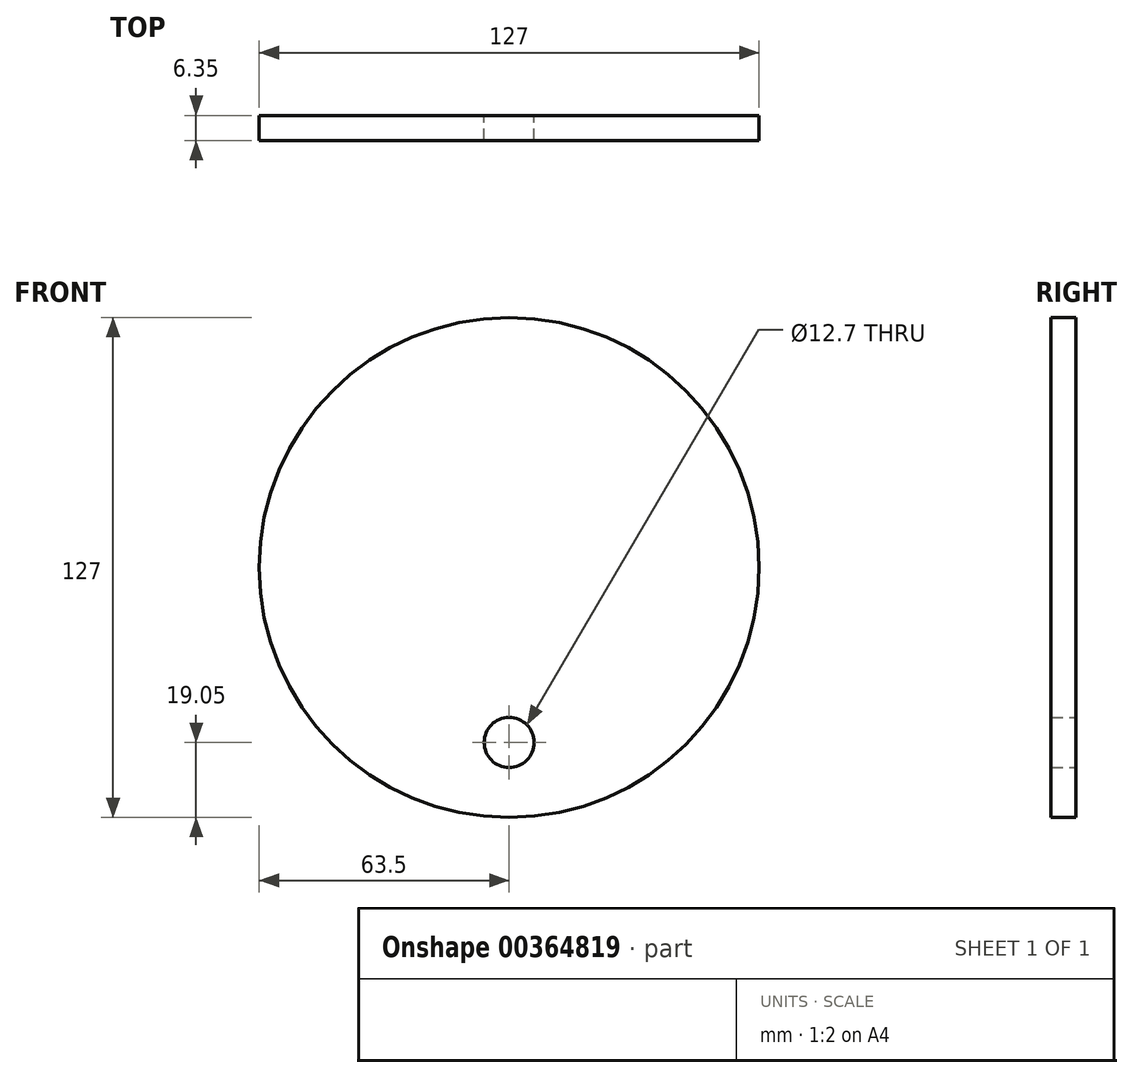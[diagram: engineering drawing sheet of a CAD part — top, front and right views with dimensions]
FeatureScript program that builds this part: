
annotation { "Feature Type Name" : "Feature", "Feature Type Description" : "" }
export const myFeature = defineFeature(function(context is Context, id is Id, definition is map)
    precondition{}
    {
        {
            var Q0;
            Q0=qCreatedBy(makeId("Front.planeOp"),FACE);
            var sketch = newSketch(context, id + "F0", { "sketchPlane" : qUnion([Q0])});
            skCircle(sketch, "E0", {"center": v(0, 0) * mm, "radius": 63.5 * mm});
            skCircle(sketch, "E1", {"center": v(0, -44.45) * mm, "radius": 6.35 * mm});
            skCircle(sketch, "E2", {"center": v(0, 0) * mm, "radius": 44.45 * mm, "construction": true});
            skSolve(sketch);
        }
        {
            var Q0;
            Q0 = qSketchRegion(id + "F0", true);
            extrude(context, id + "F1", {"entities" : qUnion([Q0]), "depth" : 6.35 * mm});
        }
    });
